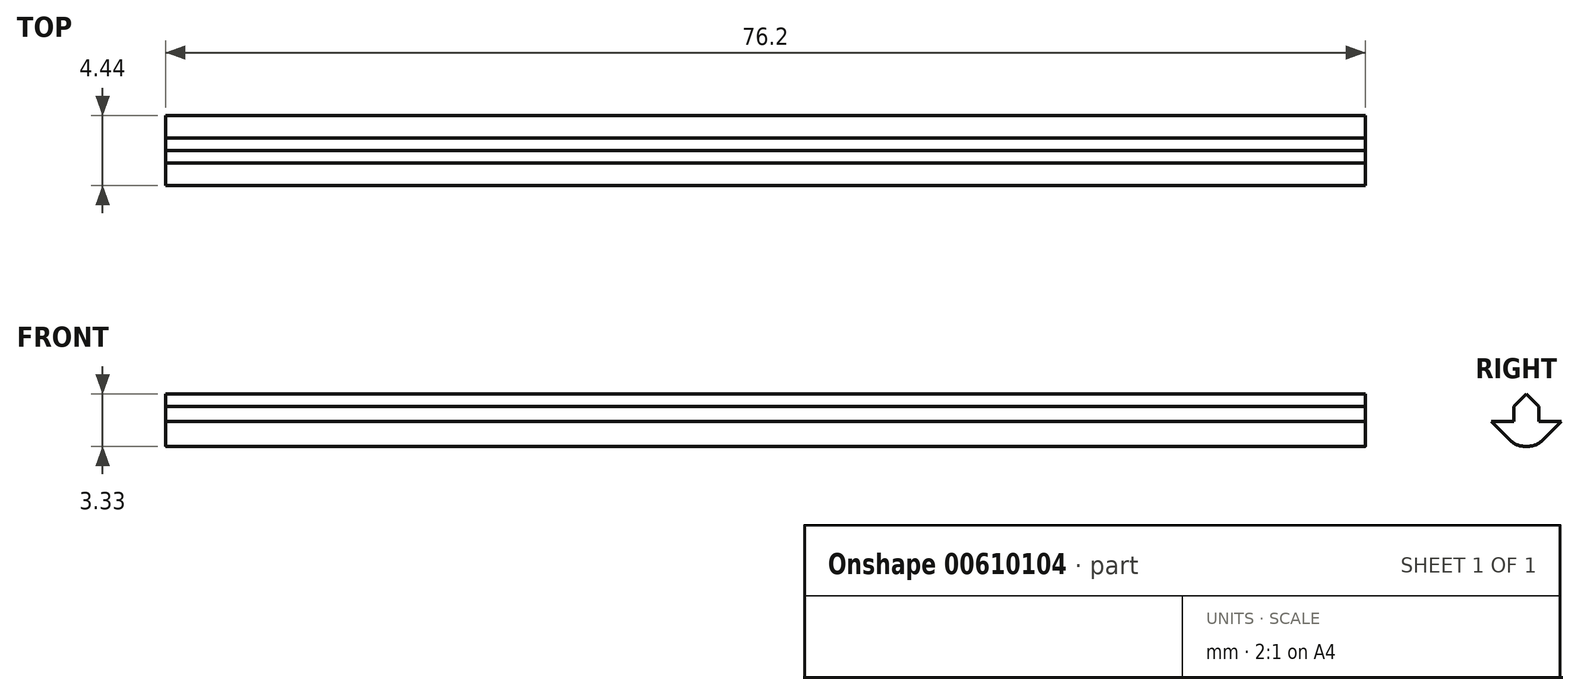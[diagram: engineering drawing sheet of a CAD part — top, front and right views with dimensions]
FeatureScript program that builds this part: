
annotation { "Feature Type Name" : "Feature", "Feature Type Description" : "" }
export const myFeature = defineFeature(function(context is Context, id is Id, definition is map)
    precondition{}
    {
        {
            var Q0;
            Q0=qCreatedBy(makeId("Top.planeOp"),FACE);
            var sketch = newSketch(context, id + "F0", { "sketchPlane" : qUnion([Q0])});
            skLineSegment(sketch, "E0.bottom", {"start": v(38.1, 3.18) * mm, "end": v(-38.1, 3.18) * mm});
            skLineSegment(sketch, "E0.top", {"start": v(38.1, -3.18) * mm, "end": v(-38.1, -3.18) * mm});
            skLineSegment(sketch, "E0.left", {"start": v(38.1, 3.18) * mm, "end": v(38.1, -3.18) * mm});
            skLineSegment(sketch, "E0.right", {"start": v(-38.1, 3.18) * mm, "end": v(-38.1, -3.18) * mm});
            skPoint(sketch, "E0.middle", {"position": v(0, 0) * mm});
            skLineSegment(sketch, "E1.bottom", {"start": v(38.1, 0.8) * mm, "end": v(-38.1, 0.8) * mm});
            skLineSegment(sketch, "E1.top", {"start": v(38.1, -0.8) * mm, "end": v(-38.1, -0.8) * mm});
            skLineSegment(sketch, "E1.left", {"start": v(38.1, 0.8) * mm, "end": v(38.1, -0.8) * mm});
            skLineSegment(sketch, "E1.right", {"start": v(-38.1, 0.8) * mm, "end": v(-38.1, -0.8) * mm});
            skSolve(sketch);
        }
        {
            var Q0;
            Q0=makeQuery(id+"F0.imprint","IMPRINT",FACE,{"disambiguationData":[TD([[makeQuery(id+"F0.imprint","IMPRINT",EDGE,{"derivedFrom":sQuery(id+"F0.wireOp",EDGE,"E1.bottom")}),1.0]])]});
            var Q1;
            {var subQ0=sQuery(id+"F0.wireOp",EDGE,"E0.top");Q1=makeQuery(id+"F0.imprint","IMPRINT",FACE,{"disambiguationData":[TD([[makeQuery(id+"F0.imprint","IMPRINT",EDGE,{"derivedFrom":subQ0}),-1.0]])]});}
            var Q2;
            {var subQ0=sQuery(id+"F0.wireOp",EDGE,"E0.bottom");Q2=makeQuery(id+"F0.imprint","IMPRINT",FACE,{"disambiguationData":[TD([[makeQuery(id+"F0.imprint","IMPRINT",EDGE,{"derivedFrom":subQ0}),1.0]])]});}
            extrude(context, id + "F1", {"entities" : qUnion([Q0, Q1, Q2]), "depth" : 1.59 * mm, "offsetDistance" : 25.4 * mm});
        }
        {
            var Q0;
            Q0=makeQuery(id+"F0.imprint","IMPRINT",FACE,{"disambiguationData":[TD([[makeQuery(id+"F0.imprint","IMPRINT",EDGE,{"derivedFrom":sQuery(id+"F0.wireOp",EDGE,"E1.bottom")}),1.0]])]});
            extrude(context, id + "F2", {"entities" : qUnion([Q0]), "operationType" : NewBodyOperationType.ADD, "depth" : 3.8 * mm, "offsetDistance" : 25.4 * mm});
        }
        {
            var Q0;
            Q0=makeQuery(id+"F2.opExtrude","CAP_EDGE",EDGE,{"disambiguationData":[OSD([sQuery(id+"F0.wireOp",EDGE,"E1.top")])],"isStart":false});
            var Q1;
            Q1=makeQuery(id+"F2.opExtrude","CAP_EDGE",EDGE,{"disambiguationData":[OSD([sQuery(id+"F0.wireOp",EDGE,"E1.bottom")])],"isStart":false});
            chamfer(context, id + "F3", {"entities" : qUnion([Q0, Q1]), "width" : 1.27 * mm, "tangentPropagation" : true});
        }
        {
            var Q0;
            Q0=makeQuery(id+"F1.opExtrude","CAP_EDGE",EDGE,{"disambiguationData":[OSD([sQuery(id+"F0.wireOp",EDGE,"E0.top")])],"isStart":true});
            var Q1;
            Q1=makeQuery(id+"F1.opExtrude","CAP_EDGE",EDGE,{"disambiguationData":[OSD([sQuery(id+"F0.wireOp",EDGE,"E0.bottom")])],"isStart":true});
            chamfer(context, id + "F4", {"entities" : qUnion([Q0, Q1]), "width" : 2.54 * mm, "tangentPropagation" : true});
        }
        {
            var Q0;
            {var subQ0=sQuery(id+"F0.wireOp",EDGE,"E0.top");Q0=makeQuery(id+"F4.opChamfer","BLEND_EDGE",EDGE,{"blendedFrom":[makeQuery(id+"F1.opExtrude","CAP_EDGE",EDGE,{"disambiguationData":[OSD([subQ0])],"isStart":true}),makeQuery(id+"F1.opExtrude","CAP_FACE",FACE,{"disambiguationData":[OSD([sQuery(id+"F0.wireOp",EDGE,"E0.bottom"),subQ0,sQuery(id+"F0.wireOp",EDGE,"E0.left"),sQuery(id+"F0.wireOp",EDGE,"E0.right"),sQuery(id+"F0.wireOp",EDGE,"E1.left"),sQuery(id+"F0.wireOp",EDGE,"E1.right")])],"isStart":true})],"blendedInto":[makeQuery(id+"F1.opExtrude","CAP_FACE",FACE,{"disambiguationData":[OSD([sQuery(id+"F0.wireOp",EDGE,"E0.bottom"),subQ0,sQuery(id+"F0.wireOp",EDGE,"E0.left"),sQuery(id+"F0.wireOp",EDGE,"E0.right"),sQuery(id+"F0.wireOp",EDGE,"E1.left"),sQuery(id+"F0.wireOp",EDGE,"E1.right")])],"isStart":true})]});}
            var Q1;
            {var subQ0=sQuery(id+"F0.wireOp",EDGE,"E0.bottom");Q1=makeQuery(id+"F4.opChamfer","BLEND_EDGE",EDGE,{"blendedFrom":[makeQuery(id+"F1.opExtrude","CAP_EDGE",EDGE,{"disambiguationData":[OSD([subQ0])],"isStart":true}),makeQuery(id+"F1.opExtrude","CAP_FACE",FACE,{"disambiguationData":[OSD([subQ0,sQuery(id+"F0.wireOp",EDGE,"E0.top"),sQuery(id+"F0.wireOp",EDGE,"E0.left"),sQuery(id+"F0.wireOp",EDGE,"E0.right"),sQuery(id+"F0.wireOp",EDGE,"E1.left"),sQuery(id+"F0.wireOp",EDGE,"E1.right")])],"isStart":true})],"blendedInto":[makeQuery(id+"F1.opExtrude","CAP_FACE",FACE,{"disambiguationData":[OSD([subQ0,sQuery(id+"F0.wireOp",EDGE,"E0.top"),sQuery(id+"F0.wireOp",EDGE,"E0.left"),sQuery(id+"F0.wireOp",EDGE,"E0.right"),sQuery(id+"F0.wireOp",EDGE,"E1.left"),sQuery(id+"F0.wireOp",EDGE,"E1.right")])],"isStart":true})]});}
            fillet(context, id + "F5", {"entities" : qUnion([Q0, Q1]), "radius" : 1.4 * mm, "tangentPropagation" : true, "allowEdgeOverflow" : false});
        }
    });
